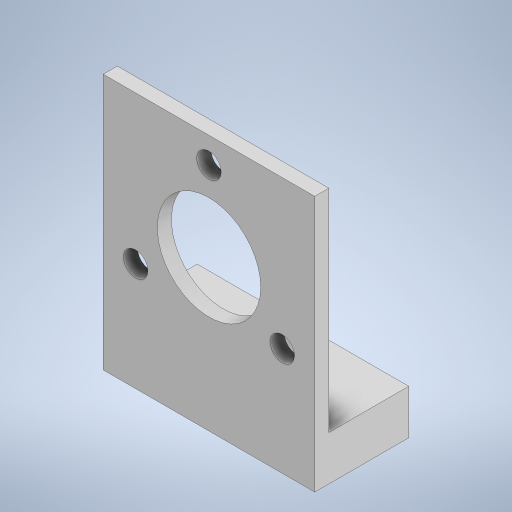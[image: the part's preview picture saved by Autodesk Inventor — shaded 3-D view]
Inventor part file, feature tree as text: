
AUTODESK INVENTOR PART (.ipt)
format: ipt  version: 2024 (Build 280153000, 153)  size: 277,504 bytes
history: native  units: in
note: dims shown in document units (in); Inventor stores cm internally (conversion verified against a paired STEP export)
features: extrude x4, sketch x4, projected_geometry x1
ambient origin geometry x8: Origin, YZ Plane, XZ Plane, XY Plane, X Axis, Y Axis, Z Axis, Center Point
bodies: Body1 (feature_tree)
feature tree (9):
  extrude  "Extrusion2"  Depth=1.7717in
  extrude  "Extrusion6"  Depth=0.6693in
  sketch  "Sketch14"  dims[d4=0.6142in d5=120.0deg]
  sketch  "Sketch15"  dims[d6=0.6142in d7=120.0deg d8=0.2047in d9=0.2047in d10=0.2047in d16=0.1181in d17=0.0in d28=1.2598in d29=0.7874in d30=0.0in d31=0.2362in d32=0.3937in d33=0.3937in d34=0.0in d35=0.2362in d36=0.0in d11=0.0197in d12=0.0344in d13=0.0197in d14=0.0344in]
  extrude  "Extrusion7"  TaperAngle=120.0deg  [1 undecoded]
  extrude  "Extrusion8"  TaperAngle=120.0deg  [1 undecoded]
  sketch  "Sketch1"  dims[d0=1.7717in d1=1.7717in]
  sketch  "Sketch13"  dims[d2=0.8661in d3=0.6693in]
  projected_geometry  "Projected Loop1"
note: 2 required parameter values undecoded (feature->parameter linkage not recoverable at this tier; creation-order binding heuristic only, values carry confidence <= 0.55)
